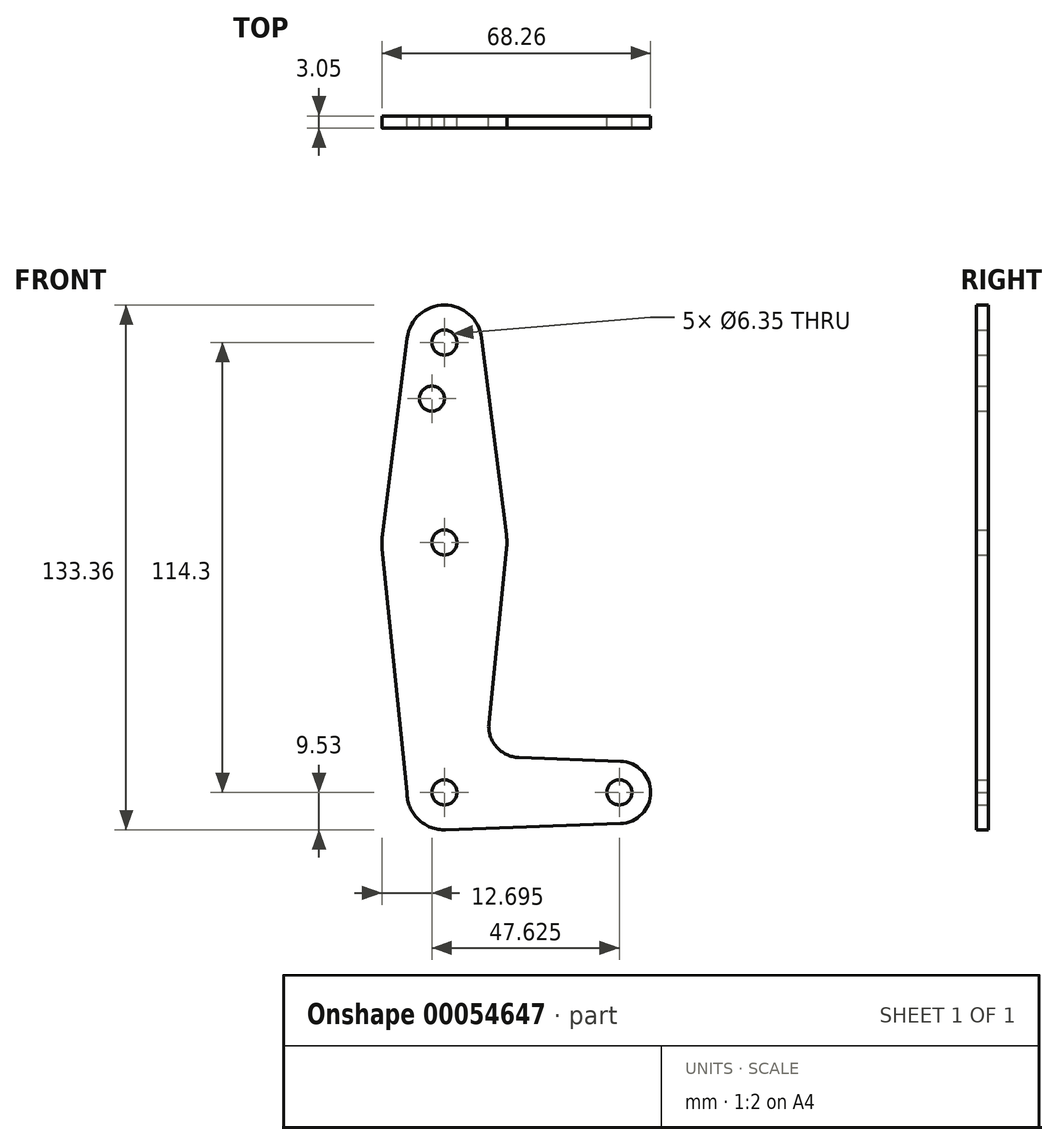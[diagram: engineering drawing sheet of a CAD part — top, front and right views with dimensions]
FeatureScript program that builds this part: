
annotation { "Feature Type Name" : "Feature", "Feature Type Description" : "" }
export const myFeature = defineFeature(function(context is Context, id is Id, definition is map)
    precondition{}
    {
        {
            var Q0;
            Q0=qCreatedBy(makeId("Front.planeOp"),FACE);
            var sketch = newSketch(context, id + "F0", { "sketchPlane" : qUnion([Q0])});
            skCircle(sketch, "E0", {"center": v(0, 114.3) * mm, "radius": 9.53 * mm});
            skCircle(sketch, "E1", {"center": v(0, 63.5) * mm, "radius": 15.88 * mm});
            skCircle(sketch, "E2", {"center": v(0, 0) * mm, "radius": 9.53 * mm});
            skCircle(sketch, "E3", {"center": v(44.45, 0) * mm, "radius": 7.94 * mm});
            skLineSegment(sketch, "E4", {"start": v(0, 114.3) * mm, "end": v(0, 0) * mm, "construction": true});
            skLineSegment(sketch, "E5", {"start": v(44.45, 0) * mm, "end": v(0, 0) * mm, "construction": true});
            skLineSegment(sketch, "E6", {"start": v(-9.45, 115.5) * mm, "end": v(-15.75, 65.48) * mm});
            skLineSegment(sketch, "E7", {"start": v(9.45, 115.5) * mm, "end": v(15.75, 65.48) * mm});
            skLineSegment(sketch, "E8", {"start": v(-9.52, 0) * mm, "end": v(-15.8, 61.9) * mm});
            skLineSegment(sketch, "E9", {"start": v(11.3, 17.6) * mm, "end": v(15.8, 61.9) * mm});
            skLineSegment(sketch, "E10", {"start": v(18.93, 8.85) * mm, "end": v(44.73, 7.93) * mm});
            skLineSegment(sketch, "E11", {"start": v(0.34, -9.52) * mm, "end": v(44.73, -7.93) * mm});
            skCircle(sketch, "E12", {"center": v(0, 114.3) * mm, "radius": 3.18 * mm});
            skCircle(sketch, "E13", {"center": v(0, 63.5) * mm, "radius": 3.18 * mm});
            skCircle(sketch, "E14", {"center": v(0, 0) * mm, "radius": 3.18 * mm});
            skCircle(sketch, "E15", {"center": v(-3.17, 100.03) * mm, "radius": 3.18 * mm});
            skCircle(sketch, "E16", {"center": v(44.45, 0) * mm, "radius": 3.18 * mm});
            skPoint(sketch, "E17.newPointB", {"position": v(0, 9.53) * mm});
            skArc(sketch, "E17.filletArc", {"start": v(11.3, 17.6) * mm, "mid": v(13.22, 11.57) * mm, "end": v(18.93, 8.85) * mm});
            skSolve(sketch);
        }
        {
            var Q0;
            Q0 = qSketchRegion(id + "F0", true);
            extrude(context, id + "F1", {"entities" : qUnion([Q0]), "depth" : 3.05 * mm});
        }
    });
